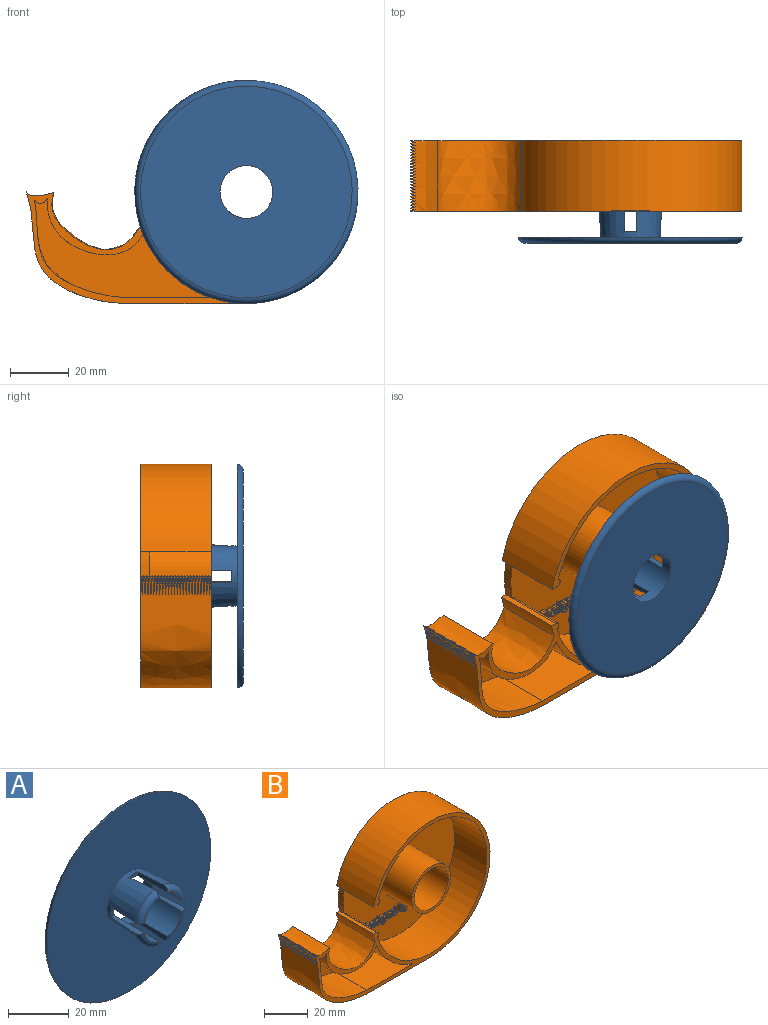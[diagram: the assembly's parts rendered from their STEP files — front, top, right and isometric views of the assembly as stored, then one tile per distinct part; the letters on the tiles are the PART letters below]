
ASSEMBLY  parts=2 mates=1
PART A: 25 faces, bbox 82.3x18x82.3 mm
  f0: cylinder r=9mm len=18mm, axis (0,1,0), area 784.4mm2, adj f1,f2,f3,f5,f7,f9,f10,f11
  f1: plane 6.91x6.79mm, normal (0,-1,0), area 1.6mm2, adj f0,f9,f19,f22
  f2: plane 6.91x6.79mm, normal (0,-1,0), area 1.6mm2, adj f0,f16,f18,f21
  f3: plane 6.91x6.79mm, normal (0,-1,0), area 1.6mm2, adj f0,f13,f15,f24
  f4: plane 76x76mm, normal (0,-1,0), area 4210.8mm2, adj f6,f8
  f5: plane 72x72mm, normal (0,1,0), area 3817mm2, adj f0,f8
  f6: cone r=11.3mm half-angle=4deg, axis (0,-1,0), area 733.2mm2, adj f4,f9,f10,f11,f12,f13,f14,f15
  f7: plane 6.91x6.79mm, normal (0,-1,0), area 1.6mm2, adj f0,f10,f12,f23
  f8: torus R=36mm, axis (0,-1,0), area 735.7mm2, adj f4,f5
  f9: plane 14.01x2.21mm, normal (1,0,0), area 24.9mm2, adj f0,f1,f6,f11,f22
  f10: plane 14.01x2.21mm, normal (-1,0,0), area 24.9mm2, adj f0,f6,f7,f11,f23
  f11: plane 4.13x1.58mm, normal (0,-1,0), area 5.5mm2, adj f0,f6,f9,f10
  f12: plane 14.01x2.21mm, normal (0,0,-1), area 24.9mm2, adj f0,f6,f7,f14,f23
  f13: plane 14.01x2.21mm, normal (0,0,1), area 24.9mm2, adj f0,f3,f6,f14,f24
  f14: plane 4.13x1.58mm, normal (0,-1,0), area 5.5mm2, adj f0,f6,f12,f13
  f15: plane 14.01x2.21mm, normal (-1,0,0), area 24.9mm2, adj f0,f3,f6,f17,f24
  f16: plane 14.01x2.21mm, normal (1,0,0), area 24.9mm2, adj f0,f2,f6,f17,f21
  f17: plane 4.13x1.58mm, normal (0,-1,0), area 5.5mm2, adj f0,f6,f15,f16
  f18: plane 14.01x2.21mm, normal (0,0,1), area 24.9mm2, adj f0,f2,f6,f20,f21
  f19: plane 14.01x2.21mm, normal (0,0,-1), area 24.9mm2, adj f0,f1,f6,f20,f22
  f20: plane 4.13x1.58mm, normal (0,-1,0), area 5.5mm2, adj f0,f6,f18,f19
  f21: torus R=9.16mm, axis (0,-1,0), area 40.3mm2, adj f2,f6,f16,f18
  f22: torus R=9.16mm, axis (0,-1,0), area 40.3mm2, adj f1,f6,f9,f19
  f23: torus R=9.16mm, axis (0,-1,0), area 40.3mm2, adj f6,f7,f10,f12
  f24: torus R=9.16mm, axis (0,-1,0), area 40.3mm2, adj f3,f6,f13,f15
PART B: 434 faces, bbox 113.9x24.1x76.1 mm
  f0: plane 72x72mm, normal (0,-1,0), area 3519.8mm2, adj f35,f36,f37,f45,f47,f103,f104,f105
  f1: extruded ~37.66x34.12mm, area 1350.7mm2, adj f3,f4,f5,f6,f7,f8,f9,f10
  f2: extruded ~24x9.46mm, area 214.6mm2, adj f40,f42,f43,f49,f50,f51,f52,f53
  f3: extruded ~0.34x0.13mm, area 0mm2, adj f1,f72,f96
  f4: extruded ~0.34x0.13mm, area 0mm2, adj f1,f43,f95
  f5: extruded ~0.34x0.13mm, area 0mm2, adj f1,f49,f93
  f6: extruded ~0.34x0.13mm, area 0mm2, adj f1,f51,f94
  f7: extruded ~0.34x0.13mm, area 0mm2, adj f1,f52,f91
  f8: extruded ~0.34x0.13mm, area 0mm2, adj f1,f53,f92
  f9: extruded ~0.34x0.13mm, area 0mm2, adj f1,f54,f89
  f10: extruded ~0.34x0.13mm, area 0mm2, adj f1,f55,f90
  f11: extruded ~0.34x0.13mm, area 0mm2, adj f1,f56,f87
  f12: extruded ~0.34x0.13mm, area 0mm2, adj f1,f57,f88
  f13: extruded ~0.34x0.13mm, area 0mm2, adj f1,f58,f85
  f14: extruded ~0.34x0.13mm, area 0mm2, adj f1,f59,f86
  f15: extruded ~0.34x0.13mm, area 0mm2, adj f1,f60,f83
  f16: extruded ~0.34x0.13mm, area 0mm2, adj f1,f61,f84
  f17: extruded ~0.34x0.13mm, area 0mm2, adj f1,f62,f81
  f18: extruded ~0.34x0.13mm, area 0mm2, adj f1,f63,f82
  f19: extruded ~0.34x0.13mm, area 0mm2, adj f1,f64,f79
  f20: extruded ~0.34x0.13mm, area 0mm2, adj f1,f65,f80
  f21: extruded ~0.34x0.13mm, area 0mm2, adj f1,f66,f77
  f22: extruded ~0.34x0.13mm, area 0mm2, adj f1,f67,f78
  f23: extruded ~0.34x0.13mm, area 0mm2, adj f1,f68,f75
  f24: extruded ~0.34x0.13mm, area 0mm2, adj f1,f69,f76
  f25: extruded ~0.34x0.13mm, area 0mm2, adj f1,f70,f73
  f26: extruded ~0.34x0.13mm, area 0mm2, adj f1,f71,f74
  f27: extruded ~0.34x0.13mm, area 0mm2, adj f1,f42,f50
  f28: extruded ~32.56x21mm, area 972mm2, adj f29,f41,f42,f48
  f29: cylinder r=38mm len=23.02mm, axis (0,1,0), area 684.6mm2, adj f28,f30,f42,f48
  f30: plane 29.41x21mm, normal (0,0,1), area 617.6mm2, adj f29,f31,f42,f48
  f31: extruded ~33.24x30.59mm, area 1096.6mm2, adj f30,f41,f42,f48
  f32: plane 40.75x24mm, normal (0,0,-1), area 978mm2, adj f1,f33,f42,f43
  f33: cylinder r=38mm len=76mm, axis (0,1,0), area 4098.6mm2, adj f32,f34,f42,f43
  f34: plane 24x2.05mm, normal (0,0,-1), area 49.2mm2, adj f33,f35,f42,f43,f47
  f35: extruded ~21x2.93mm, area 94.9mm2, adj f0,f34,f36,f42
  f36: cylinder r=36mm len=72mm, axis (0,1,0), area 4305.3mm2, adj f0,f35,f37,f42
  f37: extruded ~21x3mm, area 86mm2, adj f0,f36,f38,f42
  f38: plane 24x2.03mm, normal (0,0,1), area 48.8mm2, adj f37,f39,f42,f43,f47
  f39: cylinder r=38mm len=24mm, axis (0,1,0), area 121.5mm2, adj f38,f40,f42,f43
  f40: extruded ~30x24mm, area 1074.2mm2, adj f2,f39,f42,f43
  f41: extruded ~21x4.44mm, area 112.4mm2, adj f28,f31,f42,f48
  f42: plane 113.79x76mm, normal (0,-1,0), area 724.2mm2, adj f1,f2,f27,f28,f29,f30,f31,f32
  f43: plane 113.79x76mm, normal (0,1,0), area 5135.7mm2, adj f1,f2,f4,f32,f33,f34,f38,f39
  f44: cylinder r=11mm len=24mm, axis (0,1,0), area 1658.8mm2, adj f43,f46
  f45: cylinder r=12.5mm len=25mm, axis (0,1,0), area 1649.3mm2, adj f0,f46
  f46: plane 25x25mm, normal (0,-1,0), area 110.7mm2, adj f44,f45
  f47: cylinder r=36mm len=15mm, axis (0,1,0), area 45.3mm2, adj f0,f34,f38,f43
  f48: plane 60.85x33.7mm, normal (0,-1,0), area 726.1mm2, adj f28,f29,f30,f31,f41
  f49: plane 6.45x1.81mm, normal (-0.28,-0.96,0), area 3.7mm2, adj f1,f2,f5,f50
  f50: plane 6.45x1.81mm, normal (-0.28,0.96,0), area 3.7mm2, adj f1,f2,f27,f49
  f51: plane 6.45x1.81mm, normal (-0.28,0.96,0), area 3.7mm2, adj f1,f2,f6,f52
  f52: plane 6.45x1.81mm, normal (-0.28,-0.96,0), area 3.7mm2, adj f1,f2,f7,f51
  f53: plane 6.45x1.81mm, normal (-0.28,0.96,0), area 3.7mm2, adj f1,f2,f8,f54
  f54: plane 6.45x1.81mm, normal (-0.28,-0.96,0), area 3.7mm2, adj f1,f2,f9,f53
  f55: plane 6.45x1.81mm, normal (-0.28,0.96,0), area 3.7mm2, adj f1,f2,f10,f56
  f56: plane 6.45x1.81mm, normal (-0.28,-0.96,0), area 3.7mm2, adj f1,f2,f11,f55
  f57: plane 6.45x1.81mm, normal (-0.28,0.96,0), area 3.7mm2, adj f1,f2,f12,f58
  f58: plane 6.45x1.81mm, normal (-0.28,-0.96,0), area 3.7mm2, adj f1,f2,f13,f57
  f59: plane 6.45x1.81mm, normal (-0.28,0.96,0), area 3.7mm2, adj f1,f2,f14,f60
  f60: plane 6.45x1.81mm, normal (-0.28,-0.96,0), area 3.7mm2, adj f1,f2,f15,f59
  f61: plane 6.45x1.81mm, normal (-0.28,0.96,0), area 3.7mm2, adj f1,f2,f16,f62
  f62: plane 6.45x1.81mm, normal (-0.28,-0.96,0), area 3.7mm2, adj f1,f2,f17,f61
  f63: plane 6.45x1.81mm, normal (-0.28,0.96,0), area 3.7mm2, adj f1,f2,f18,f64
  f64: plane 6.45x1.81mm, normal (-0.28,-0.96,0), area 3.7mm2, adj f1,f2,f19,f63
  f65: plane 6.45x1.81mm, normal (-0.28,0.96,0), area 3.7mm2, adj f1,f2,f20,f66
  f66: plane 6.45x1.81mm, normal (-0.28,-0.96,0), area 3.7mm2, adj f1,f2,f21,f65
  f67: plane 6.45x1.81mm, normal (-0.28,0.96,0), area 3.7mm2, adj f1,f2,f22,f68
  f68: plane 6.45x1.81mm, normal (-0.28,-0.96,0), area 3.7mm2, adj f1,f2,f23,f67
  f69: plane 6.45x1.81mm, normal (-0.28,0.96,0), area 3.7mm2, adj f1,f2,f24,f70
  f70: plane 6.45x1.81mm, normal (-0.28,-0.96,0), area 3.7mm2, adj f1,f2,f25,f69
  f71: plane 6.45x1.81mm, normal (-0.28,0.96,0), area 3.7mm2, adj f1,f2,f26,f72
  f72: plane 6.45x1.81mm, normal (-0.28,-0.96,0), area 3.7mm2, adj f1,f2,f3,f71
  f73: plane 6.45x1.81mm, normal (-0.28,0.96,0), area 3.7mm2, adj f1,f2,f25,f74
  f74: plane 6.45x1.81mm, normal (-0.28,-0.96,0), area 3.7mm2, adj f1,f2,f26,f73
  f75: plane 6.45x1.81mm, normal (-0.28,0.96,0), area 3.7mm2, adj f1,f2,f23,f76
  f76: plane 6.45x1.81mm, normal (-0.28,-0.96,0), area 3.7mm2, adj f1,f2,f24,f75
  f77: plane 6.45x1.81mm, normal (-0.28,0.96,0), area 3.7mm2, adj f1,f2,f21,f78
  f78: plane 6.45x1.81mm, normal (-0.28,-0.96,0), area 3.7mm2, adj f1,f2,f22,f77
  f79: plane 6.45x1.81mm, normal (-0.28,0.96,0), area 3.7mm2, adj f1,f2,f19,f80
  f80: plane 6.45x1.81mm, normal (-0.28,-0.96,0), area 3.7mm2, adj f1,f2,f20,f79
  f81: plane 6.45x1.81mm, normal (-0.28,0.96,0), area 3.7mm2, adj f1,f2,f17,f82
  f82: plane 6.45x1.81mm, normal (-0.28,-0.96,0), area 3.7mm2, adj f1,f2,f18,f81
  f83: plane 6.45x1.81mm, normal (-0.28,0.96,0), area 3.7mm2, adj f1,f2,f15,f84
  f84: plane 6.45x1.81mm, normal (-0.28,-0.96,0), area 3.7mm2, adj f1,f2,f16,f83
  f85: plane 6.45x1.81mm, normal (-0.28,0.96,0), area 3.7mm2, adj f1,f2,f13,f86
  f86: plane 6.45x1.81mm, normal (-0.28,-0.96,0), area 3.7mm2, adj f1,f2,f14,f85
  f87: plane 6.45x1.81mm, normal (-0.28,0.96,0), area 3.7mm2, adj f1,f2,f11,f88
  f88: plane 6.45x1.81mm, normal (-0.28,-0.96,0), area 3.7mm2, adj f1,f2,f12,f87
  f89: plane 6.45x1.81mm, normal (-0.28,0.96,0), area 3.7mm2, adj f1,f2,f9,f90
  f90: plane 6.45x1.81mm, normal (-0.28,-0.96,0), area 3.7mm2, adj f1,f2,f10,f89
  f91: plane 6.45x1.81mm, normal (-0.28,0.96,0), area 3.7mm2, adj f1,f2,f7,f92
  f92: plane 6.45x1.81mm, normal (-0.28,-0.96,0), area 3.7mm2, adj f1,f2,f8,f91
  f93: plane 6.45x1.81mm, normal (-0.28,0.96,0), area 3.7mm2, adj f1,f2,f5,f94
  f94: plane 6.45x1.81mm, normal (-0.28,-0.96,0), area 3.7mm2, adj f1,f2,f6,f93
  f95: plane 6.45x1.81mm, normal (-0.28,-0.96,0), area 3.7mm2, adj f1,f2,f4,f96
  f96: plane 6.45x1.81mm, normal (-0.28,0.96,0), area 3.7mm2, adj f1,f2,f3,f95
  f97: extruded ~2x0.98mm, area 2.1mm2, adj f98,f110,f111,f112
  f98: extruded ~2x1.01mm, area 2.2mm2, adj f97,f99,f111,f112
  f99: extruded ~2x1.04mm, area 2.2mm2, adj f98,f100,f111,f112
  f100: plane 2x0.47mm, normal (0,0,1), area 0.9mm2, adj f99,f101,f111,f112
  f101: plane 2.66x2mm, normal (1,0,0), area 5.3mm2, adj f100,f102,f111,f112
  f102: plane 2x0.56mm, normal (0,0,-1), area 1.1mm2, adj f101,f110,f111,f112
  f103: extruded ~2x1.26mm, area 2.7mm2, adj f0,f104,f109,f111
  f104: extruded ~2x1.2mm, area 2.6mm2, adj f0,f103,f105,f111
  f105: extruded ~2x1.21mm, area 2.6mm2, adj f0,f104,f106,f111
  f106: plane 2x1.02mm, normal (0,0,1), area 2mm2, adj f0,f105,f107,f111
  f107: plane 3.33x2mm, normal (-1,0,0), area 6.7mm2, adj f0,f106,f108,f111
  f108: plane 2x0.92mm, normal (0,0,-1), area 1.8mm2, adj f0,f107,f109,f111
  f109: extruded ~2x1.29mm, area 2.8mm2, adj f0,f103,f108,f111
  f110: extruded ~2x0.97mm, area 2.1mm2, adj f97,f102,f111,f112
  f111: plane 3.33x2.66mm, normal (0,-1,0), area 3.5mm2, adj f97,f98,f99,f100,f101,f102,f103,f104
  f112: plane 2.66x1.86mm, normal (0,-1,0), area 4.3mm2, adj f97,f98,f99,f100,f101,f102,f110
  f113: extruded ~2x0.48mm, area 1.1mm2, adj f114,f131,f132,f133
  f114: extruded ~2x0.46mm, area 1mm2, adj f113,f115,f132,f133
  f115: extruded ~2x0.55mm, area 1.2mm2, adj f114,f116,f132,f133
  f116: plane 2x1.3mm, normal (0,0,1), area 2.6mm2, adj f115,f131,f132,f133
  f117: extruded ~2x0.87mm, area 1.9mm2, adj f0,f118,f130,f132
  f118: extruded ~2x0.43mm, area 0.9mm2, adj f0,f117,f119,f132
  f119: extruded ~2x0.38mm, area 0.8mm2, adj f0,f118,f120,f132
  f120: plane 2x0.34mm, normal (1,0,0), area 0.7mm2, adj f0,f119,f121,f132
  f121: extruded ~2x0.8mm, area 1.6mm2, adj f0,f120,f122,f132
  f122: extruded ~2x0.59mm, area 1.3mm2, adj f0,f121,f123,f132
  f123: extruded ~2x0.67mm, area 1.4mm2, adj f0,f122,f124,f132
  f124: plane 2x1.72mm, normal (0,0,-1), area 3.4mm2, adj f0,f123,f125,f132
  f125: plane 2x0.24mm, normal (1,0,0), area 0.5mm2, adj f0,f124,f126,f132
  f126: extruded ~2x0.81mm, area 1.8mm2, adj f0,f125,f127,f132
  f127: extruded ~2x0.74mm, area 1.7mm2, adj f0,f126,f128,f132
  f128: extruded ~2x0.8mm, area 1.8mm2, adj f0,f127,f129,f132
  f129: extruded ~2x0.96mm, area 2.1mm2, adj f0,f128,f130,f132
  f130: extruded ~2x0.94mm, area 2mm2, adj f0,f117,f129,f132
  f131: extruded ~2x0.54mm, area 1.2mm2, adj f113,f116,f132,f133
  f132: plane 2.59x2.11mm, normal (0,-1,0), area 2.5mm2, adj f113,f114,f115,f116,f117,f118,f119,f120
  f133: plane 1.3x0.74mm, normal (0,-1,0), area 0.8mm2, adj f113,f114,f115,f116,f131
  f134: extruded ~2x0.54mm, area 1.2mm2, adj f0,f135,f158,f159
  f135: extruded ~2x0.41mm, area 0.9mm2, adj f0,f134,f136,f159
  f136: extruded ~2x0.6mm, area 1.4mm2, adj f0,f135,f137,f159
  f137: extruded ~2x0.44mm, area 0.9mm2, adj f0,f136,f138,f159
  f138: extruded ~2x0.17mm, area 0.4mm2, adj f0,f137,f139,f159
  f139: extruded ~2x0.17mm, area 0.4mm2, adj f0,f138,f140,f159
  f140: extruded ~2x0.23mm, area 0.6mm2, adj f0,f139,f141,f159
  f141: extruded ~2x0.41mm, area 0.8mm2, adj f0,f140,f142,f159
  f142: extruded ~2x0.68mm, area 1.4mm2, adj f0,f141,f143,f159
  f143: plane 2x0.31mm, normal (0.92,0,-0.4), area 0.7mm2, adj f0,f142,f144,f159
  f144: extruded ~2x0.79mm, area 1.6mm2, adj f0,f143,f145,f159
  f145: extruded ~2x0.68mm, area 1.4mm2, adj f0,f144,f146,f159
  f146: extruded ~2x0.48mm, area 1.1mm2, adj f0,f145,f147,f159
  f147: extruded ~2x0.29mm, area 0.6mm2, adj f0,f146,f148,f159
  f148: extruded ~2x0.22mm, area 0.6mm2, adj f0,f147,f149,f159
  f149: extruded ~2x0.5mm, area 1.1mm2, adj f0,f148,f150,f159
  f150: extruded ~2x0.49mm, area 1.1mm2, adj f0,f149,f151,f159
  f151: extruded ~2x0.25mm, area 0.6mm2, adj f0,f150,f152,f159
  f152: extruded ~2x0.29mm, area 0.7mm2, adj f0,f151,f153,f159
  f153: extruded ~2x0.46mm, area 0.9mm2, adj f0,f152,f154,f159
  f154: extruded ~2x0.4mm, area 0.8mm2, adj f0,f153,f155,f159
  f155: extruded ~2x0.39mm, area 0.8mm2, adj f0,f154,f156,f159
  f156: plane 2x0.35mm, normal (-1,0,0), area 0.7mm2, adj f0,f155,f157,f159
  f157: extruded ~2x0.77mm, area 1.6mm2, adj f0,f156,f158,f159
  f158: extruded ~2x0.73mm, area 1.5mm2, adj f0,f134,f157,f159
  f159: plane 2.59x1.77mm, normal (0,-1,0), area 1.9mm2, adj f134,f135,f136,f137,f138,f139,f140,f141
  f160: plane 2x0.38mm, normal (0,0,-1), area 0.8mm2, adj f0,f161,f163,f164
  f161: plane 2.5x2mm, normal (1,0,0), area 5mm2, adj f0,f160,f162,f164
  f162: plane 2x0.38mm, normal (0,0,1), area 0.8mm2, adj f0,f161,f163,f164
  f163: plane 2.5x2mm, normal (-1,0,0), area 5mm2, adj f0,f160,f162,f164
  f164: plane 2.5x0.38mm, normal (0,-1,0), area 0.9mm2, adj f160,f161,f162,f163
  f165: extruded ~2x0.19mm, area 0.4mm2, adj f0,f166,f172,f173
  f166: extruded ~2x0.19mm, area 0.4mm2, adj f0,f165,f167,f173
  f167: extruded ~2x0.16mm, area 0.4mm2, adj f0,f166,f168,f173
  f168: extruded ~2x0.16mm, area 0.3mm2, adj f0,f167,f169,f173
  f169: extruded ~2x0.19mm, area 0.4mm2, adj f0,f168,f170,f173
  f170: extruded ~2x0.19mm, area 0.4mm2, adj f0,f169,f171,f173
  f171: extruded ~2x0.16mm, area 0.3mm2, adj f0,f170,f172,f173
  f172: extruded ~2x0.16mm, area 0.4mm2, adj f0,f165,f171,f173
  f173: plane 0.5x0.45mm, normal (0,-1,0), area 0.2mm2, adj f165,f166,f167,f168,f169,f170,f171,f172
  f174: extruded ~2x0.4mm, area 0.9mm2, adj f175,f217,f218,f219
  f175: extruded ~2x0.43mm, area 0.9mm2, adj f174,f176,f218,f219
  f176: extruded ~2x0.41mm, area 0.9mm2, adj f175,f177,f218,f219
  f177: extruded ~2x0.56mm, area 1.8mm2, adj f176,f178,f218,f219
  f178: extruded ~2x0.55mm, area 1.8mm2, adj f177,f217,f218,f219
  f179: extruded ~2x0.31mm, area 0.7mm2, adj f180,f215,f218,f220
  f180: extruded ~2x0.35mm, area 0.8mm2, adj f179,f181,f218,f220
  f181: extruded ~2x0.4mm, area 0.9mm2, adj f180,f182,f218,f220
  f182: plane 2x0.45mm, normal (0,0,-1), area 0.9mm2, adj f181,f183,f218,f220
  f183: extruded ~2x0.47mm, area 1mm2, adj f182,f184,f218,f220
  f184: extruded ~2x0.28mm, area 0.6mm2, adj f183,f185,f218,f220
  f185: extruded ~2x0.39mm, area 0.9mm2, adj f184,f186,f218,f220
  f186: extruded ~2x0.7mm, area 1.5mm2, adj f185,f215,f218,f220
  f187: plane 2x0.24mm, normal (1,0,0), area 0.5mm2, adj f0,f188,f216,f218
  f188: plane 2x0.86mm, normal (0,0,1), area 1.7mm2, adj f0,f187,f189,f218
  f189: extruded ~2x0.35mm, area 0.7mm2, adj f0,f188,f190,f218
  f190: extruded ~2x0.7mm, area 1.5mm2, adj f0,f189,f191,f218
  f191: extruded ~2x0.63mm, area 1.4mm2, adj f0,f190,f192,f218
  f192: extruded ~2x0.44mm, area 0.9mm2, adj f0,f191,f193,f218
  f193: extruded ~2x0.32mm, area 0.8mm2, adj f0,f192,f194,f218
  f194: extruded ~2x0.23mm, area 0.6mm2, adj f0,f193,f195,f218
  f195: extruded ~2x0.24mm, area 0.5mm2, adj f0,f194,f196,f218
  f196: extruded ~2x0.21mm, area 0.5mm2, adj f0,f195,f197,f218
  f197: extruded ~2x0.16mm, area 0.4mm2, adj f0,f196,f198,f218
  f198: extruded ~2x0.41mm, area 1mm2, adj f0,f197,f199,f218
  f199: extruded ~2x0.39mm, area 0.9mm2, adj f0,f198,f200,f218
  f200: extruded ~2x0.52mm, area 1.2mm2, adj f0,f199,f201,f218
  f201: extruded ~2x0.75mm, area 1.6mm2, adj f0,f200,f202,f218
  f202: extruded ~2x0.97mm, area 2mm2, adj f0,f201,f203,f218
  f203: extruded ~2x0.63mm, area 1.5mm2, adj f0,f202,f204,f218
  f204: extruded ~2x0.5mm, area 1.1mm2, adj f0,f203,f205,f218
  f205: extruded ~2x0.62mm, area 1.3mm2, adj f0,f204,f206,f218
  f206: plane 2x0.44mm, normal (0,0,1), area 0.9mm2, adj f0,f205,f207,f218
  f207: extruded ~2x0.29mm, area 0.6mm2, adj f0,f206,f208,f218
  f208: extruded ~2x0.15mm, area 0.4mm2, adj f0,f207,f209,f218
  f209: extruded ~2x0.32mm, area 0.8mm2, adj f0,f208,f210,f218
  f210: extruded ~2x0.21mm, area 0.4mm2, adj f0,f209,f211,f218
  f211: extruded ~2x0.69mm, area 1.5mm2, adj f0,f210,f212,f218
  f212: extruded ~2x0.59mm, area 1.3mm2, adj f0,f211,f213,f218
  f213: extruded ~2x0.29mm, area 0.6mm2, adj f0,f212,f214,f218
  f214: extruded ~2x0.21mm, area 0.5mm2, adj f0,f213,f216,f218
  f215: extruded ~2x0.49mm, area 1mm2, adj f179,f186,f218,f220
  f216: plane 2x0.46mm, normal (0.12,0,-0.99), area 0.9mm2, adj f0,f187,f214,f218
  f217: extruded ~2x0.41mm, area 0.9mm2, adj f174,f178,f218,f219
  f218: plane 3.66x2.35mm, normal (0,-1,0), area 3.6mm2, adj f174,f175,f176,f177,f178,f179,f180,f181
  f219: plane 1.11x1.1mm, normal (0,-1,0), area 1mm2, adj f174,f175,f176,f177,f178,f217
  f220: plane 1.59x0.89mm, normal (0,-1,0), area 1.2mm2, adj f179,f180,f181,f182,f183,f184,f185,f186
  f221: plane 2x1.61mm, normal (-1,0,0), area 3.2mm2, adj f0,f222,f237,f238
  f222: plane 2x0.38mm, normal (0,0,-1), area 0.8mm2, adj f0,f221,f223,f238
  f223: plane 2x1.63mm, normal (1,0,0), area 3.3mm2, adj f0,f222,f224,f238
  f224: extruded ~2x0.7mm, area 1.5mm2, adj f0,f223,f225,f238
  f225: extruded ~2x0.68mm, area 1.5mm2, adj f0,f224,f226,f238
  f226: extruded ~2x0.47mm, area 1mm2, adj f0,f225,f227,f238
  f227: extruded ~2x0.33mm, area 0.9mm2, adj f0,f226,f228,f238
  f228: plane 2x0.02mm, normal (0,0,1), area 0mm2, adj f0,f227,f229,f238
  f229: plane 2x0.34mm, normal (0.98,0,0.18), area 0.7mm2, adj f0,f228,f230,f238
  f230: plane 2x0.31mm, normal (0,0,1), area 0.6mm2, adj f0,f229,f231,f238
  f231: plane 2.5x2mm, normal (-1,0,0), area 5mm2, adj f0,f230,f232,f238
  f232: plane 2x0.38mm, normal (0,0,-1), area 0.8mm2, adj f0,f231,f233,f238
  f233: plane 2x1.31mm, normal (1,0,0), area 2.6mm2, adj f0,f232,f234,f238
  f234: extruded ~2x0.7mm, area 1.5mm2, adj f0,f233,f235,f238
  f235: extruded ~2x0.57mm, area 1.3mm2, adj f0,f234,f236,f238
  f236: extruded ~2x0.44mm, area 0.9mm2, adj f0,f235,f237,f238
  f237: extruded ~2x0.46mm, area 1mm2, adj f0,f221,f236,f238
  f238: plane 2.54x2.09mm, normal (0,-1,0), area 2.3mm2, adj f221,f222,f223,f224,f225,f226,f227,f228
  f239: extruded ~2x0.48mm, area 1.1mm2, adj f240,f257,f258,f259
  f240: extruded ~2x0.46mm, area 1mm2, adj f239,f241,f258,f259
  f241: extruded ~2x0.55mm, area 1.2mm2, adj f240,f242,f258,f259
  f242: plane 2x1.3mm, normal (0,0,1), area 2.6mm2, adj f241,f257,f258,f259
  f243: extruded ~2x0.87mm, area 1.9mm2, adj f0,f244,f256,f258
  f244: extruded ~2x0.43mm, area 0.9mm2, adj f0,f243,f245,f258
  f245: extruded ~2x0.38mm, area 0.8mm2, adj f0,f244,f246,f258
  f246: plane 2x0.34mm, normal (1,0,0), area 0.7mm2, adj f0,f245,f247,f258
  f247: extruded ~2x0.8mm, area 1.6mm2, adj f0,f246,f248,f258
  f248: extruded ~2x0.59mm, area 1.3mm2, adj f0,f247,f249,f258
  f249: extruded ~2x0.67mm, area 1.4mm2, adj f0,f248,f250,f258
  f250: plane 2x1.72mm, normal (0,0,-1), area 3.4mm2, adj f0,f249,f251,f258
  f251: plane 2x0.24mm, normal (1,0,0), area 0.5mm2, adj f0,f250,f252,f258
  f252: extruded ~2x0.81mm, area 1.8mm2, adj f0,f251,f253,f258
  f253: extruded ~2x0.74mm, area 1.7mm2, adj f0,f252,f254,f258
  f254: extruded ~2x0.8mm, area 1.8mm2, adj f0,f253,f255,f258
  f255: extruded ~2x0.96mm, area 2.1mm2, adj f0,f254,f256,f258
  f256: extruded ~2x0.94mm, area 2mm2, adj f0,f243,f255,f258
  f257: extruded ~2x0.54mm, area 1.2mm2, adj f239,f242,f258,f259
  f258: plane 2.59x2.11mm, normal (0,-1,0), area 2.5mm2, adj f239,f240,f241,f242,f243,f244,f245,f246
  f259: plane 1.3x0.74mm, normal (0,-1,0), area 0.8mm2, adj f239,f240,f241,f242,f257
  f260: extruded ~2x0.56mm, area 1.2mm2, adj f261,f283,f284,f285
  f261: extruded ~2x0.51mm, area 1.2mm2, adj f260,f262,f284,f285
  f262: extruded ~2x0.72mm, area 1.5mm2, adj f261,f263,f284,f285
  f263: extruded ~2x0.73mm, area 1.5mm2, adj f262,f264,f284,f285
  f264: extruded ~2x0.51mm, area 1.2mm2, adj f263,f265,f284,f285
  f265: extruded ~2x0.56mm, area 1.3mm2, adj f264,f266,f284,f285
  f266: extruded ~2x0.76mm, area 1.6mm2, adj f265,f267,f284,f285
  f267: plane 2x0.08mm, normal (-1,0,0), area 0.2mm2, adj f266,f283,f284,f285
  f268: plane 2x0.02mm, normal (0,0,-1), area 0mm2, adj f0,f269,f282,f284
  f269: plane 2x0.33mm, normal (-0.99,0,-0.15), area 0.7mm2, adj f0,f268,f270,f284
  f270: plane 2x0.31mm, normal (0,0,-1), area 0.6mm2, adj f0,f269,f271,f284
  f271: plane 3.54x2mm, normal (1,0,0), area 7.1mm2, adj f0,f270,f272,f284
  f272: plane 2x0.38mm, normal (0,0,1), area 0.8mm2, adj f0,f271,f273,f284
  f273: plane 2x1.02mm, normal (-1,0,0), area 2mm2, adj f0,f272,f274,f284
  f274: plane 2x0.18mm, normal (-1,0,-0.05), area 0.4mm2, adj f0,f273,f275,f284
  f275: plane 2x0.18mm, normal (-1,0,-0.09), area 0.4mm2, adj f0,f274,f276,f284
  f276: plane 2x0.03mm, normal (0,0,1), area 0.1mm2, adj f0,f275,f277,f284
  f277: extruded ~2x0.78mm, area 1.8mm2, adj f0,f276,f278,f284
  f278: extruded ~2x0.76mm, area 1.7mm2, adj f0,f277,f279,f284
  f279: extruded ~2x0.96mm, area 2mm2, adj f0,f278,f280,f284
  f280: extruded ~2x0.95mm, area 2mm2, adj f0,f279,f281,f284
  f281: extruded ~2x0.76mm, area 1.7mm2, adj f0,f280,f282,f284
  f282: extruded ~2x0.78mm, area 1.8mm2, adj f0,f268,f281,f284
  f283: extruded ~2x0.68mm, area 1.4mm2, adj f260,f267,f284,f285
  f284: plane 3.59x2.2mm, normal (0,-1,0), area 3mm2, adj f260,f261,f262,f263,f264,f265,f266,f267
  f285: plane 1.95x1.43mm, normal (0,-1,0), area 2.3mm2, adj f260,f261,f262,f263,f264,f265,f266,f267
  f286: extruded ~2x0.56mm, area 1.2mm2, adj f287,f308,f309,f310
  f287: extruded ~2x0.53mm, area 1.2mm2, adj f286,f288,f309,f310
  f288: extruded ~2x0.73mm, area 1.5mm2, adj f287,f289,f309,f310
  f289: extruded ~2x0.73mm, area 1.5mm2, adj f288,f290,f309,f310
  f290: extruded ~2x0.52mm, area 1.2mm2, adj f289,f291,f309,f310
  f291: extruded ~2x0.56mm, area 1.3mm2, adj f290,f292,f309,f310
  f292: extruded ~2x0.75mm, area 1.6mm2, adj f291,f308,f309,f310
  f293: extruded ~2x0.76mm, area 1.7mm2, adj f0,f294,f307,f309
  f294: extruded ~2x0.78mm, area 1.8mm2, adj f0,f293,f295,f309
  f295: plane 2x0.02mm, normal (0,0,1), area 0mm2, adj f0,f294,f296,f309
  f296: extruded ~2x0.52mm, area 1mm2, adj f0,f295,f297,f309
  f297: plane 2x0.86mm, normal (1,0,0), area 1.7mm2, adj f0,f296,f298,f309
  f298: plane 2x0.38mm, normal (0,0,1), area 0.8mm2, adj f0,f297,f299,f309
  f299: plane 3.54x2mm, normal (-1,0,0), area 7.1mm2, adj f0,f298,f300,f309
  f300: plane 2x0.27mm, normal (0,0,-1), area 0.5mm2, adj f0,f299,f301,f309
  f301: plane 2x0.32mm, normal (0.97,0,-0.24), area 0.7mm2, adj f0,f300,f302,f309
  f302: plane 2x0.03mm, normal (0,0,-1), area 0.1mm2, adj f0,f301,f303,f309
  f303: extruded ~2x0.34mm, area 0.9mm2, adj f0,f302,f304,f309
  f304: extruded ~2x0.45mm, area 0.9mm2, adj f0,f303,f305,f309
  f305: extruded ~2x0.76mm, area 1.7mm2, adj f0,f304,f306,f309
  f306: extruded ~2x0.96mm, area 2mm2, adj f0,f305,f307,f309
  f307: extruded ~2x0.95mm, area 2mm2, adj f0,f293,f306,f309
  f308: extruded ~2x0.75mm, area 1.6mm2, adj f286,f292,f309,f310
  f309: plane 3.59x2.2mm, normal (0,-1,0), area 3mm2, adj f286,f287,f288,f289,f290,f291,f292,f293
  f310: plane 1.95x1.43mm, normal (0,-1,0), area 2.3mm2, adj f286,f287,f288,f289,f290,f291,f292,f308
  f311: plane 2x0.41mm, normal (0,0,1), area 0.8mm2, adj f0,f312,f326,f327
  f312: plane 2.51x2mm, normal (-0.93,0,-0.37), area 5.4mm2, adj f0,f311,f313,f327
  f313: plane 2x0.35mm, normal (-0.93,0,0.37), area 0.8mm2, adj f0,f312,f314,f327
  f314: extruded ~2x0.56mm, area 1.5mm2, adj f0,f313,f315,f327
  f315: extruded ~2x0.28mm, area 0.6mm2, adj f0,f314,f316,f327
  f316: plane 2x0.3mm, normal (-1,0,0), area 0.6mm2, adj f0,f315,f317,f327
  f317: extruded ~2x0.34mm, area 0.7mm2, adj f0,f316,f318,f327
  f318: extruded ~2x0.52mm, area 1.1mm2, adj f0,f317,f319,f327
  f319: extruded ~2x0.6mm, area 1.4mm2, adj f0,f318,f320,f327
  f320: plane 2.84x2mm, normal (0.94,0,-0.35), area 6.1mm2, adj f0,f319,f321,f327
  f321: plane 2x0.41mm, normal (0,0,1), area 0.8mm2, adj f0,f320,f322,f327
  f322: extruded ~2x1.73mm, area 3.7mm2, adj f0,f321,f323,f327
  f323: extruded ~2x0.4mm, area 0.8mm2, adj f0,f322,f324,f327
  f324: plane 2x0.02mm, normal (0,0,1), area 0mm2, adj f0,f323,f325,f327
  f325: extruded ~2x0.7mm, area 1.5mm2, adj f0,f324,f326,f327
  f326: plane 2x1.42mm, normal (0.93,0,0.36), area 3mm2, adj f0,f311,f325,f327
  f327: plane 3.62x2.34mm, normal (0,-1,0), area 2.4mm2, adj f311,f312,f313,f314,f315,f316,f317,f318
  f328: plane 2x1.03mm, normal (-0.94,0,-0.35), area 2.2mm2, adj f329,f340,f341,f342
  f329: plane 2x1.08mm, normal (0,0,1), area 2.2mm2, adj f328,f330,f341,f342
  f330: plane 2x1.03mm, normal (0.94,0,-0.35), area 2.2mm2, adj f329,f331,f341,f342
  f331: extruded ~2x0.48mm, area 1mm2, adj f330,f340,f341,f342
  f332: plane 2x1.06mm, normal (-0.93,0,-0.36), area 2.3mm2, adj f0,f333,f339,f341
  f333: plane 2x0.4mm, normal (0,0,-1), area 0.8mm2, adj f0,f332,f334,f341
  f334: plane 3.34x2mm, normal (0.93,0,0.36), area 7.2mm2, adj f0,f333,f335,f341
  f335: plane 2x0.33mm, normal (0,0,1), area 0.7mm2, adj f0,f334,f336,f341
  f336: plane 3.34x2mm, normal (-0.93,0,0.37), area 7.2mm2, adj f0,f335,f337,f341
  f337: plane 2x0.39mm, normal (0,0,-1), area 0.8mm2, adj f0,f336,f338,f341
  f338: plane 2x1.06mm, normal (0.93,0,-0.36), area 2.3mm2, adj f0,f337,f339,f341
  f339: plane 2x1.33mm, normal (0,0,-1), area 2.7mm2, adj f0,f332,f338,f341
  f340: extruded ~2x0.48mm, area 1mm2, adj f328,f331,f341,f342
  f341: plane 3.34x2.95mm, normal (0,-1,0), area 2.9mm2, adj f328,f329,f330,f331,f332,f333,f334,f335
  f342: plane 1.51x1.08mm, normal (0,-1,0), area 0.8mm2, adj f328,f329,f330,f331,f340
  f343: plane 2x1.61mm, normal (-1,0,0), area 3.2mm2, adj f0,f344,f359,f360
  f344: plane 2x0.38mm, normal (0,0,-1), area 0.8mm2, adj f0,f343,f345,f360
  f345: plane 2x1.63mm, normal (1,0,0), area 3.3mm2, adj f0,f344,f346,f360
  f346: extruded ~2x0.7mm, area 1.5mm2, adj f0,f345,f347,f360
  f347: extruded ~2x0.68mm, area 1.5mm2, adj f0,f346,f348,f360
  f348: extruded ~2x0.47mm, area 1mm2, adj f0,f347,f349,f360
  f349: extruded ~2x0.33mm, area 0.9mm2, adj f0,f348,f350,f360
  f350: plane 2x0.02mm, normal (0,0,1), area 0mm2, adj f0,f349,f351,f360
  f351: plane 2x0.34mm, normal (0.98,0,0.18), area 0.7mm2, adj f0,f350,f352,f360
  f352: plane 2x0.31mm, normal (0,0,1), area 0.6mm2, adj f0,f351,f353,f360
  f353: plane 2.5x2mm, normal (-1,0,0), area 5mm2, adj f0,f352,f354,f360
  f354: plane 2x0.38mm, normal (0,0,-1), area 0.8mm2, adj f0,f353,f355,f360
  f355: plane 2x1.31mm, normal (1,0,0), area 2.6mm2, adj f0,f354,f356,f360
  f356: extruded ~2x0.7mm, area 1.5mm2, adj f0,f355,f357,f360
  f357: extruded ~2x0.57mm, area 1.3mm2, adj f0,f356,f358,f360
  f358: extruded ~2x0.44mm, area 0.9mm2, adj f0,f357,f359,f360
  f359: extruded ~2x0.46mm, area 1mm2, adj f0,f343,f358,f360
  f360: plane 2.54x2.09mm, normal (0,-1,0), area 2.3mm2, adj f343,f344,f345,f346,f347,f348,f349,f350
  f361: extruded ~2x0.4mm, area 0.9mm2, adj f362,f404,f405,f406
  f362: extruded ~2x0.43mm, area 0.9mm2, adj f361,f363,f405,f406
  f363: extruded ~2x0.41mm, area 0.9mm2, adj f362,f364,f405,f406
  f364: extruded ~2x0.56mm, area 1.8mm2, adj f363,f365,f405,f406
  f365: extruded ~2x0.55mm, area 1.8mm2, adj f364,f404,f405,f406
  f366: extruded ~2x0.31mm, area 0.7mm2, adj f367,f402,f405,f407
  f367: extruded ~2x0.35mm, area 0.8mm2, adj f366,f368,f405,f407
  f368: extruded ~2x0.4mm, area 0.9mm2, adj f367,f369,f405,f407
  f369: plane 2x0.45mm, normal (0,0,-1), area 0.9mm2, adj f368,f370,f405,f407
  f370: extruded ~2x0.47mm, area 1mm2, adj f369,f371,f405,f407
  f371: extruded ~2x0.28mm, area 0.6mm2, adj f370,f372,f405,f407
  f372: extruded ~2x0.39mm, area 0.9mm2, adj f371,f373,f405,f407
  f373: extruded ~2x0.7mm, area 1.5mm2, adj f372,f402,f405,f407
  f374: plane 2x0.24mm, normal (1,0,0), area 0.5mm2, adj f0,f375,f403,f405
  f375: plane 2x0.86mm, normal (0,0,1), area 1.7mm2, adj f0,f374,f376,f405
  f376: extruded ~2x0.35mm, area 0.7mm2, adj f0,f375,f377,f405
  f377: extruded ~2x0.7mm, area 1.5mm2, adj f0,f376,f378,f405
  f378: extruded ~2x0.63mm, area 1.4mm2, adj f0,f377,f379,f405
  f379: extruded ~2x0.44mm, area 0.9mm2, adj f0,f378,f380,f405
  f380: extruded ~2x0.32mm, area 0.8mm2, adj f0,f379,f381,f405
  f381: extruded ~2x0.23mm, area 0.6mm2, adj f0,f380,f382,f405
  f382: extruded ~2x0.24mm, area 0.5mm2, adj f0,f381,f383,f405
  f383: extruded ~2x0.21mm, area 0.5mm2, adj f0,f382,f384,f405
  f384: extruded ~2x0.16mm, area 0.4mm2, adj f0,f383,f385,f405
  f385: extruded ~2x0.41mm, area 1mm2, adj f0,f384,f386,f405
  f386: extruded ~2x0.39mm, area 0.9mm2, adj f0,f385,f387,f405
  f387: extruded ~2x0.52mm, area 1.2mm2, adj f0,f386,f388,f405
  f388: extruded ~2x0.75mm, area 1.6mm2, adj f0,f387,f389,f405
  f389: extruded ~2x0.97mm, area 2mm2, adj f0,f388,f390,f405
  f390: extruded ~2x0.63mm, area 1.5mm2, adj f0,f389,f391,f405
  f391: extruded ~2x0.5mm, area 1.1mm2, adj f0,f390,f392,f405
  f392: extruded ~2x0.62mm, area 1.3mm2, adj f0,f391,f393,f405
  f393: plane 2x0.44mm, normal (0,0,1), area 0.9mm2, adj f0,f392,f394,f405
  f394: extruded ~2x0.29mm, area 0.6mm2, adj f0,f393,f395,f405
  f395: extruded ~2x0.15mm, area 0.4mm2, adj f0,f394,f396,f405
  f396: extruded ~2x0.32mm, area 0.8mm2, adj f0,f395,f397,f405
  f397: extruded ~2x0.21mm, area 0.4mm2, adj f0,f396,f398,f405
  f398: extruded ~2x0.69mm, area 1.5mm2, adj f0,f397,f399,f405
  f399: extruded ~2x0.59mm, area 1.3mm2, adj f0,f398,f400,f405
  f400: extruded ~2x0.29mm, area 0.6mm2, adj f0,f399,f401,f405
  f401: extruded ~2x0.21mm, area 0.5mm2, adj f0,f400,f403,f405
  f402: extruded ~2x0.49mm, area 1mm2, adj f366,f373,f405,f407
  f403: plane 2x0.46mm, normal (0.12,0,-0.99), area 0.9mm2, adj f0,f374,f401,f405
  f404: extruded ~2x0.41mm, area 0.9mm2, adj f361,f365,f405,f406
  f405: plane 3.66x2.35mm, normal (0,-1,0), area 3.6mm2, adj f361,f362,f363,f364,f365,f366,f367,f368
  f406: plane 1.11x1.1mm, normal (0,-1,0), area 1mm2, adj f361,f362,f363,f364,f365,f404
  f407: plane 1.59x0.89mm, normal (0,-1,0), area 1.2mm2, adj f366,f367,f368,f369,f370,f371,f372,f373
  f408: extruded ~2x0.48mm, area 1.1mm2, adj f409,f426,f427,f428
  f409: extruded ~2x0.46mm, area 1mm2, adj f408,f410,f427,f428
  f410: extruded ~2x0.55mm, area 1.2mm2, adj f409,f411,f427,f428
  f411: plane 2x1.3mm, normal (0,0,1), area 2.6mm2, adj f410,f426,f427,f428
  f412: extruded ~2x0.87mm, area 1.9mm2, adj f0,f413,f425,f427
  f413: extruded ~2x0.43mm, area 0.9mm2, adj f0,f412,f414,f427
  f414: extruded ~2x0.38mm, area 0.8mm2, adj f0,f413,f415,f427
  f415: plane 2x0.34mm, normal (1,0,0), area 0.7mm2, adj f0,f414,f416,f427
  f416: extruded ~2x0.8mm, area 1.6mm2, adj f0,f415,f417,f427
  f417: extruded ~2x0.59mm, area 1.3mm2, adj f0,f416,f418,f427
  f418: extruded ~2x0.67mm, area 1.4mm2, adj f0,f417,f419,f427
  f419: plane 2x1.72mm, normal (0,0,-1), area 3.4mm2, adj f0,f418,f420,f427
  f420: plane 2x0.24mm, normal (1,0,0), area 0.5mm2, adj f0,f419,f421,f427
  f421: extruded ~2x0.81mm, area 1.8mm2, adj f0,f420,f422,f427
  f422: extruded ~2x0.74mm, area 1.7mm2, adj f0,f421,f423,f427
  f423: extruded ~2x0.8mm, area 1.8mm2, adj f0,f422,f424,f427
  f424: extruded ~2x0.96mm, area 2.1mm2, adj f0,f423,f425,f427
  f425: extruded ~2x0.94mm, area 2mm2, adj f0,f412,f424,f427
  f426: extruded ~2x0.54mm, area 1.2mm2, adj f408,f411,f427,f428
  f427: plane 2.59x2.11mm, normal (0,-1,0), area 2.5mm2, adj f408,f409,f410,f411,f412,f413,f414,f415
  f428: plane 1.3x0.74mm, normal (0,-1,0), area 0.8mm2, adj f408,f409,f410,f411,f426
  f429: plane 2x0.38mm, normal (0,0,-1), area 0.8mm2, adj f0,f430,f432,f433
  f430: plane 3.54x2mm, normal (1,0,0), area 7.1mm2, adj f0,f429,f431,f433
  f431: plane 2x0.38mm, normal (0,0,1), area 0.8mm2, adj f0,f430,f432,f433
  f432: plane 3.54x2mm, normal (-1,0,0), area 7.1mm2, adj f0,f429,f431,f433
  f433: plane 3.54x0.38mm, normal (0,-1,0), area 1.3mm2, adj f429,f430,f431,f432
PLACE A rot(axis=(0,0,-1),180deg) t=(-101.7,-331.97,12.79)mm
PLACE B t=(-101.7,-297.03,12.79)mm
MATE slider A.f6 <-> B.f45  axis (0,1,0) through (-101.7,-316.11,12.79)mm
